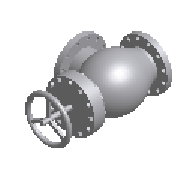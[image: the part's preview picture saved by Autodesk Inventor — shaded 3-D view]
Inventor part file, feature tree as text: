
AUTODESK INVENTOR PART (.ipt)
format: ipt  version: 2024 (Build 280153000, 153)  size: 377,344 bytes
history: native  units: mm (DEFAULTED — no unit token found)
features: other x9, extrude x8, pattern_circular x3, revolve x2, sketch x2, plane x1
ambient origin geometry x8: Origin, YZ Plane, XZ Plane, XY Plane, X Axis, Y Axis, Z Axis, Center Point
bodies: Body1 (feature_tree), Body2 (feature_tree)
feature tree (25):
  revolve  "Revolution1"  [1 undecoded]
  extrude  "Extrusion1"  Depth=25.4mm
  pattern_circular  "Circular Pattern1"  [2 undecoded]
  revolve  "Revolution2"  Angle=90.0deg
  extrude  "Extrusion2"  Depth=25.4mm
  extrude  "Extrusion3"  Depth=25.4mm
  plane  "Work Plane1"
  extrude  "Extrusion4"  Depth=25.4mm TaperAngle=0.0deg
  pattern_circular  "Circular Pattern2"  Count=4  [1 undecoded]
  extrude  "Extrusion5"  TaperAngle=360.0deg  [1 undecoded]
  extrude  "Extrusion6"  Depth=25.4mm
  pattern_circular  "Circular Pattern4"  [2 undecoded]
  other  "Work Axis2"
  other  "Work Point1"
  other  "Work Axis3"
  other  "Work Point2"
  other  "Suprimir cara1"
  other  "Suprimir cara2"
  other  "Suprimir cara3"
  other  "Suprimir cara4"
  extrude  "Extrusión7"  Depth=25.4mm
  extrude  "Extrusión8"  Depth=25.4mm
  sketch  "Boceto9"  dims[d0=50.8mm d1=123.952mm]
  other  "Sólido2"
  sketch  "Boceto10"  dims[d2=1.524mm d3=17.526mm d4=35.052mm d7=90.0deg d5=88.9mm d6=19.05mm d10=25.4mm d8=0.0mm d9=40.0mm d11=360.0deg d12=35.052mm d14=88.265mm d15=139.7mm d16=203.2mm d17=6.985mm d18=13.97mm d19=13.97mm d24=90.0deg d20=6.985mm d21=120.0deg d22=4.656667mm d23=4.656667mm d25=30.0mm d34=360.0deg d36=25.4mm d26=0.0mm d27=25.4mm d28=101.6mm d29=0.0mm d30=88.9mm d31=22.86mm d32=8.763mm d35=52.578mm d37=0.0mm d38=40.0mm d39=360.0deg d40=101.6mm d41=1.524mm d42=50.8mm d43=123.952mm d44=17.526mm d45=101.6mm d48=35.3695mm d49=71.12mm d50=35.052mm d53=25.4mm d67=25.4mm d54=0.0mm d55=45.0deg d71=8.763mm d72=45.0deg d73=19.05mm d74=88.9mm d75=25.4mm d76=0.0mm d77=40.0mm d78=360.0deg d80=25.4mm d81=0.0mm d82=25.4mm d83=0.0mm]
note: 7 required parameter values undecoded (feature->parameter linkage not recoverable at this tier; creation-order binding heuristic only, values carry confidence <= 0.55)